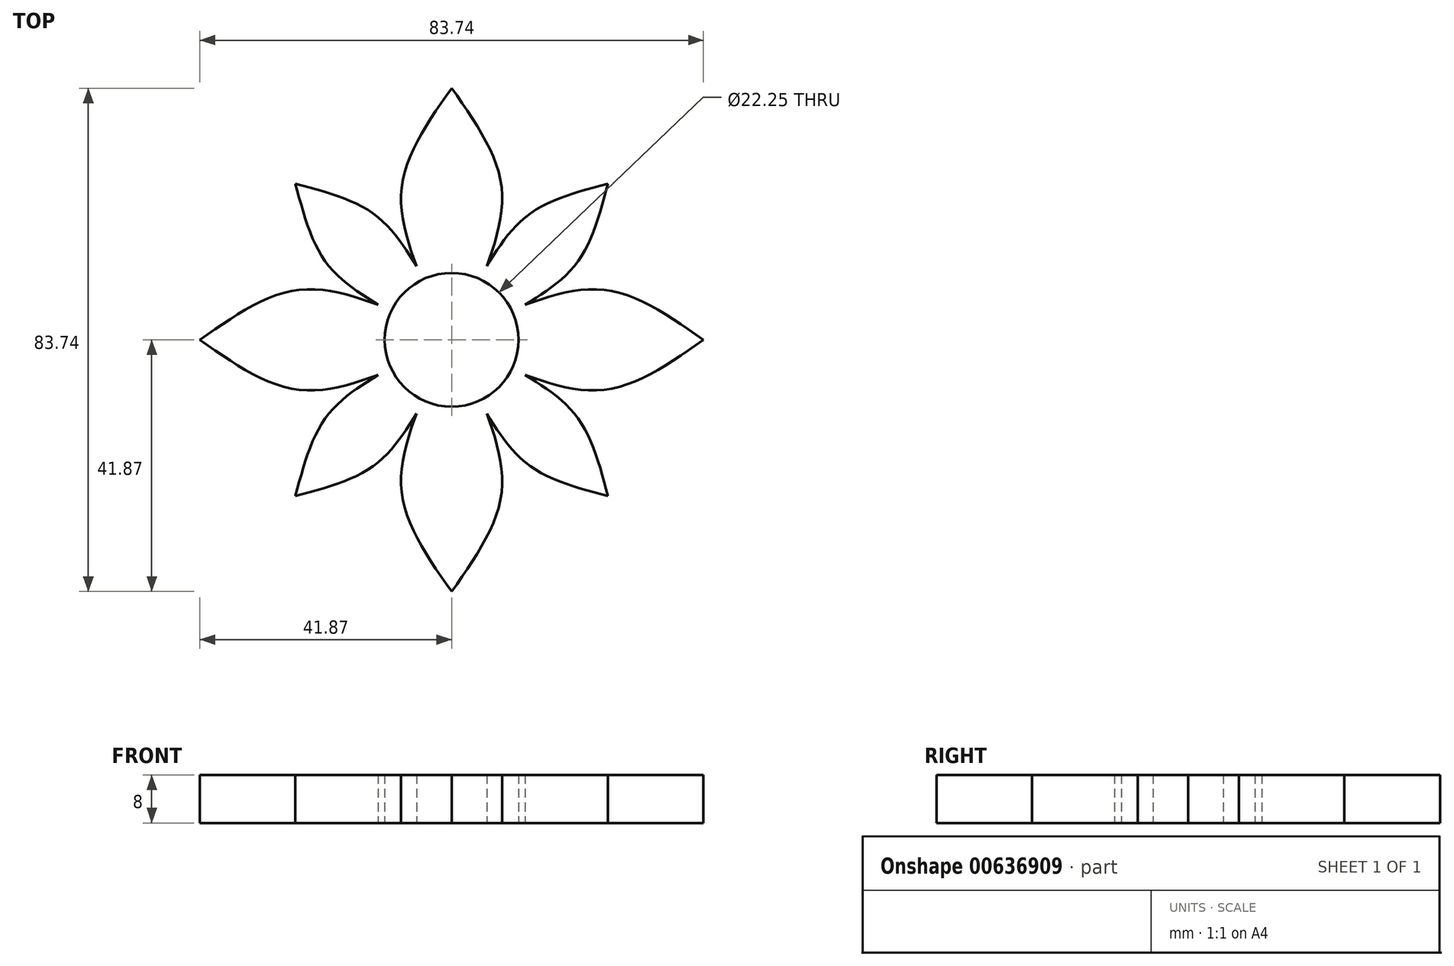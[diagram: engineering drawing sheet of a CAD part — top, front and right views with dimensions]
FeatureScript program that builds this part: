
annotation { "Feature Type Name" : "Feature", "Feature Type Description" : "" }
export const myFeature = defineFeature(function(context is Context, id is Id, definition is map)
    precondition{}
    {
        {
            var Q0;
            Q0=qCreatedBy(makeId("Top.planeOp"),FACE);
            var sketch = newSketch(context, id + "F0", { "sketchPlane" : qUnion([Q0])});
            skCircle(sketch, "E0", {"center": v(0, 0) * mm, "radius": 11.12 * mm});
            skCircle(sketch, "E1.cCircle", {"center": v(0, 26.05) * mm, "radius": 4.7 * mm, "construction": true});
            skLineSegment(sketch, "E1.0", {"start": v(5.41, 26.33) * mm, "end": v(2.95, 21.5) * mm});
            skLineSegment(sketch, "E1.1", {"start": v(2.95, 21.5) * mm, "end": v(-2.46, 21.22) * mm});
            skLineSegment(sketch, "E1.2", {"start": v(-2.46, 21.22) * mm, "end": v(-5.41, 25.77) * mm});
            skLineSegment(sketch, "E1.3", {"start": v(-5.41, 25.77) * mm, "end": v(-2.95, 30.6) * mm});
            skLineSegment(sketch, "E1.4", {"start": v(-2.95, 30.6) * mm, "end": v(2.46, 30.87) * mm});
            skLineSegment(sketch, "E1.5", {"start": v(2.46, 30.87) * mm, "end": v(5.41, 26.33) * mm});
            skPoint(sketch, "E1.0.midPoint", {"position": v(4.18, 23.91) * mm});
            skPoint(sketch, "E2.1.0", {"position": v(-23.91, 4.18) * mm});
            skCircle(sketch, "E2.1.1", {"center": v(-26.05, 0) * mm, "radius": 4.7 * mm, "construction": true});
            skLineSegment(sketch, "E2.1.2", {"start": v(-30.6, -2.95) * mm, "end": v(-30.87, 2.46) * mm});
            skLineSegment(sketch, "E2.1.3", {"start": v(-26.33, 5.41) * mm, "end": v(-21.5, 2.95) * mm});
            skLineSegment(sketch, "E2.1.4", {"start": v(-21.5, 2.95) * mm, "end": v(-21.22, -2.46) * mm});
            skLineSegment(sketch, "E2.1.5", {"start": v(-21.22, -2.46) * mm, "end": v(-25.77, -5.41) * mm});
            skLineSegment(sketch, "E2.1.6", {"start": v(-25.77, -5.41) * mm, "end": v(-30.6, -2.95) * mm});
            skLineSegment(sketch, "E2.1.7", {"start": v(-30.87, 2.46) * mm, "end": v(-26.33, 5.41) * mm});
            skPoint(sketch, "E2.2.0", {"position": v(-4.18, -23.91) * mm});
            skCircle(sketch, "E2.2.1", {"center": v(0, -26.05) * mm, "radius": 4.7 * mm, "construction": true});
            skLineSegment(sketch, "E2.2.2", {"start": v(2.95, -30.6) * mm, "end": v(-2.46, -30.87) * mm});
            skLineSegment(sketch, "E2.2.3", {"start": v(-5.41, -26.33) * mm, "end": v(-2.95, -21.5) * mm});
            skLineSegment(sketch, "E2.2.4", {"start": v(-2.95, -21.5) * mm, "end": v(2.46, -21.22) * mm});
            skLineSegment(sketch, "E2.2.5", {"start": v(2.46, -21.22) * mm, "end": v(5.41, -25.77) * mm});
            skLineSegment(sketch, "E2.2.6", {"start": v(5.41, -25.77) * mm, "end": v(2.95, -30.6) * mm});
            skLineSegment(sketch, "E2.2.7", {"start": v(-2.46, -30.87) * mm, "end": v(-5.41, -26.33) * mm});
            skPoint(sketch, "E2.3.0", {"position": v(23.91, -4.18) * mm});
            skCircle(sketch, "E2.3.1", {"center": v(26.05, 0) * mm, "radius": 4.7 * mm, "construction": true});
            skLineSegment(sketch, "E2.3.2", {"start": v(30.6, 2.95) * mm, "end": v(30.87, -2.46) * mm});
            skLineSegment(sketch, "E2.3.3", {"start": v(26.33, -5.41) * mm, "end": v(21.5, -2.95) * mm});
            skLineSegment(sketch, "E2.3.4", {"start": v(21.5, -2.95) * mm, "end": v(21.22, 2.46) * mm});
            skLineSegment(sketch, "E2.3.5", {"start": v(21.22, 2.46) * mm, "end": v(25.77, 5.41) * mm});
            skLineSegment(sketch, "E2.3.6", {"start": v(25.77, 5.41) * mm, "end": v(30.6, 2.95) * mm});
            skLineSegment(sketch, "E2.3.7", {"start": v(30.87, -2.46) * mm, "end": v(26.33, -5.41) * mm});
            skFitSpline(sketch, "E3", {"points": [v(-4.98, 9.95) * mm, v(-8.27, 25.7) * mm, v(0, 41.87) * mm], "startDerivative": vector(-12.29, 32.71) * mm, "endDerivative": vector(21.92, 31.12) * mm});
            skFitSpline(sketch, "E4.MirrorCS", {"points": [v(-4.98, 9.95) * mm, v(-8.27, 25.7) * mm, v(0, 41.87) * mm], "startDerivative": vector(-12.29, 32.71) * mm, "endDerivative": vector(21.92, 31.12) * mm});
            skFitSpline(sketch, "E5.MirrorCS", {"points": [v(-4.98, -9.95) * mm, v(-8.27, -25.7) * mm, v(0, -41.87) * mm], "startDerivative": vector(-12.29, -32.71) * mm, "endDerivative": vector(21.92, -31.12) * mm});
            skFitSpline(sketch, "E6.MirrorCS", {"points": [v(4.98, -9.95) * mm, v(8.27, -25.7) * mm, v(0, -41.87) * mm], "startDerivative": vector(12.29, -32.71) * mm, "endDerivative": vector(-21.92, -31.12) * mm});
            skFitSpline(sketch, "E7.MirrorCS", {"points": [v(4.98, -9.95) * mm, v(8.27, -25.7) * mm, v(0, -41.87) * mm], "startDerivative": vector(12.29, -32.71) * mm, "endDerivative": vector(-21.92, -31.12) * mm});
            skFitSpline(sketch, "E8.MirrorCS", {"points": [v(4.98, -9.95) * mm, v(8.27, -25.7) * mm, v(0, -41.87) * mm], "startDerivative": vector(12.29, -32.71) * mm, "endDerivative": vector(-21.92, -31.12) * mm});
            skFitSpline(sketch, "E9.MirrorCS", {"points": [v(-9.95, -4.98) * mm, v(-25.7, -8.27) * mm, v(-41.87, 0) * mm], "startDerivative": vector(-32.71, -12.29) * mm, "endDerivative": vector(-31.12, 21.92) * mm});
            skFitSpline(sketch, "E10.MirrorCS", {"points": [v(-9.95, 4.98) * mm, v(-25.7, 8.27) * mm, v(-41.87, 0) * mm], "startDerivative": vector(-32.71, 12.29) * mm, "endDerivative": vector(-31.12, -21.92) * mm});
            skFitSpline(sketch, "E11.MirrorCS", {"points": [v(9.95, 4.98) * mm, v(25.7, 8.27) * mm, v(41.87, 0) * mm], "startDerivative": vector(32.71, 12.29) * mm, "endDerivative": vector(31.12, -21.92) * mm});
            skFitSpline(sketch, "E12.MirrorCS", {"points": [v(9.95, -4.98) * mm, v(25.7, -8.27) * mm, v(41.87, 0) * mm], "startDerivative": vector(32.71, -12.29) * mm, "endDerivative": vector(31.12, 21.92) * mm});
            skFitSpline(sketch, "E13.MirrorCS", {"points": [v(4.98, 9.95) * mm, v(8.27, 25.7) * mm, v(0, 41.87) * mm], "startDerivative": vector(12.29, 32.71) * mm, "endDerivative": vector(-21.92, 31.12) * mm});
            skCircle(sketch, "E14", {"center": v(0, 0) * mm, "radius": 13.56 * mm});
            skPoint(sketch, "E15", {"position": v(12.24, 5.84) * mm});
            skPoint(sketch, "E16", {"position": v(5.84, 12.24) * mm});
            skPoint(sketch, "E17.1.internal.snap0", {"position": v(13, 13) * mm});
            skFitSpline(sketch, "E17", {"points": [v(5.84, 12.24) * mm, v(13, 20.97) * mm, v(25.99, 25.99) * mm], "startDerivative": vector(12.84, 20.52) * mm, "endDerivative": vector(27.2, 7.2) * mm});
            skFitSpline(sketch, "E18.MirrorCS", {"points": [v(12.24, 5.84) * mm, v(20.97, 13) * mm, v(25.99, 25.99) * mm], "startDerivative": vector(20.52, 12.84) * mm, "endDerivative": vector(7.2, 27.2) * mm});
            skFitSpline(sketch, "E19.MirrorCS", {"points": [v(-5.84, 12.24) * mm, v(-13, 20.97) * mm, v(-25.99, 25.99) * mm], "startDerivative": vector(-12.84, 20.52) * mm, "endDerivative": vector(-27.2, 7.2) * mm});
            skFitSpline(sketch, "E20.MirrorCS", {"points": [v(-12.24, 5.84) * mm, v(-20.97, 13) * mm, v(-25.99, 25.99) * mm], "startDerivative": vector(-20.52, 12.84) * mm, "endDerivative": vector(-7.2, 27.2) * mm});
            skFitSpline(sketch, "E21.MirrorCS", {"points": [v(-12.24, -5.84) * mm, v(-20.97, -13) * mm, v(-25.99, -25.99) * mm], "startDerivative": vector(-20.52, -12.84) * mm, "endDerivative": vector(-7.2, -27.2) * mm});
            skFitSpline(sketch, "E22.MirrorCS", {"points": [v(-5.84, -12.24) * mm, v(-13, -20.97) * mm, v(-25.99, -25.99) * mm], "startDerivative": vector(-12.84, -20.52) * mm, "endDerivative": vector(-27.2, -7.2) * mm});
            skFitSpline(sketch, "E23.MirrorCS", {"points": [v(5.84, -12.24) * mm, v(13, -20.97) * mm, v(25.99, -25.99) * mm], "startDerivative": vector(12.84, -20.52) * mm, "endDerivative": vector(27.2, -7.2) * mm});
            skFitSpline(sketch, "E24.MirrorCS", {"points": [v(12.24, -5.84) * mm, v(20.97, -13) * mm, v(25.99, -25.99) * mm], "startDerivative": vector(20.52, -12.84) * mm, "endDerivative": vector(7.2, -27.2) * mm});
            skSolve(sketch);
        }
        {
            var Q0;
            Q0=makeQuery(id+"F0.imprint","IMPRINT",FACE,{"disambiguationData":[TD([[makeQuery(id+"F0.imprint","IMPRINT",EDGE,{"derivedFrom":sQuery(id+"F0.wireOp",EDGE,"E2.1.2")}),-1.0]])]});
            var Q1;
            {var subQ5=sQuery(id+"F0.wireOp",EDGE,"E17");Q1=makeQuery(id+"F0.imprint","IMPRINT",FACE,{"disambiguationData":[TD([[makeQuery(id+"F0.imprint","IMPRINT",EDGE,{"derivedFrom":subQ5}),-1.0]])]});}
            var Q2;
            Q2=makeQuery(id+"F0.imprint","IMPRINT",FACE,{"disambiguationData":[TD([[makeQuery(id+"F0.imprint","IMPRINT",EDGE,{"derivedFrom":sQuery(id+"F0.wireOp",EDGE,"E2.2.2")}),-1.0]])]});
            var Q3;
            {var subQ0=sQuery(id+"F0.wireOp",EDGE,"E8.MirrorCS");var subQ1=sQuery(id+"F0.wireOp",EDGE,"E0");var subQ2=makeQuery(id+"F0.imprint","INTERSECT",VERTEX,{"derivedFrom":[subQ1,subQ0]});Q3=makeQuery(id+"F0.imprint","IMPRINT",FACE,{"disambiguationData":[TD([[makeQuery(id+"F0.imprint","IMPRINT",EDGE,{"disambiguationData":[TD([[subQ2,-1.0]])],"derivedFrom":subQ1}),-1.0]])]});}
            var Q4;
            {var subQ5=sQuery(id+"F0.wireOp",EDGE,"E23.MirrorCS");Q4=makeQuery(id+"F0.imprint","IMPRINT",FACE,{"disambiguationData":[TD([[makeQuery(id+"F0.imprint","IMPRINT",EDGE,{"derivedFrom":subQ5}),1.0]])]});}
            var Q5;
            Q5=makeQuery(id+"F0.imprint","IMPRINT",FACE,{"disambiguationData":[TD([[makeQuery(id+"F0.imprint","IMPRINT",EDGE,{"derivedFrom":sQuery(id+"F0.wireOp",EDGE,"E2.2.2")}),1.0]])]});
            var Q6;
            Q6=makeQuery(id+"F0.imprint","IMPRINT",FACE,{"disambiguationData":[TD([[makeQuery(id+"F0.imprint","IMPRINT",EDGE,{"derivedFrom":sQuery(id+"F0.wireOp",EDGE,"E1.0")}),1.0]])]});
            var Q7;
            Q7=makeQuery(id+"F0.imprint","IMPRINT",FACE,{"disambiguationData":[TD([[makeQuery(id+"F0.imprint","IMPRINT",EDGE,{"derivedFrom":sQuery(id+"F0.wireOp",EDGE,"E2.3.2")}),-1.0]])]});
            var Q8;
            {var subQ0=sQuery(id+"F0.wireOp",EDGE,"E11.MirrorCS");var subQ1=sQuery(id+"F0.wireOp",EDGE,"E0");var subQ2=makeQuery(id+"F0.imprint","INTERSECT",VERTEX,{"derivedFrom":[subQ1,subQ0]});Q8=makeQuery(id+"F0.imprint","IMPRINT",FACE,{"disambiguationData":[TD([[makeQuery(id+"F0.imprint","IMPRINT",EDGE,{"disambiguationData":[TD([[subQ2,1.0]])],"derivedFrom":subQ1}),-1.0]])]});}
            var Q9;
            {var subQ0=sQuery(id+"F0.wireOp",EDGE,"E5.MirrorCS");var subQ1=sQuery(id+"F0.wireOp",EDGE,"E0");var subQ2=makeQuery(id+"F0.imprint","INTERSECT",VERTEX,{"derivedFrom":[subQ1,subQ0]});Q9=makeQuery(id+"F0.imprint","IMPRINT",FACE,{"disambiguationData":[TD([[makeQuery(id+"F0.imprint","IMPRINT",EDGE,{"disambiguationData":[TD([[subQ2,-1.0]])],"derivedFrom":subQ1}),-1.0]])]});}
            var Q10;
            {var subQ0=sQuery(id+"F0.wireOp",EDGE,"E0");var subQ4=makeQuery(id+"F0.imprint","INTERSECT",VERTEX,{"derivedFrom":[subQ0,sQuery(id+"F0.wireOp",EDGE,"E13.MirrorCS")]});Q10=makeQuery(id+"F0.imprint","IMPRINT",FACE,{"disambiguationData":[TD([[makeQuery(id+"F0.imprint","IMPRINT",EDGE,{"disambiguationData":[TD([[subQ4,1.0]])],"derivedFrom":subQ0}),1.0]])]});}
            var Q11;
            {var subQ0=sQuery(id+"F0.wireOp",EDGE,"E5.MirrorCS");var subQ1=sQuery(id+"F0.wireOp",EDGE,"E0");var subQ2=makeQuery(id+"F0.imprint","INTERSECT",VERTEX,{"derivedFrom":[subQ1,subQ0]});Q11=makeQuery(id+"F0.imprint","IMPRINT",FACE,{"disambiguationData":[TD([[makeQuery(id+"F0.imprint","IMPRINT",EDGE,{"disambiguationData":[TD([[subQ2,1.0]])],"derivedFrom":subQ1}),-1.0]])]});}
            var Q12;
            {var subQ5=sQuery(id+"F0.wireOp",EDGE,"E22.MirrorCS");Q12=makeQuery(id+"F0.imprint","IMPRINT",FACE,{"disambiguationData":[TD([[makeQuery(id+"F0.imprint","IMPRINT",EDGE,{"derivedFrom":subQ5}),-1.0]])]});}
            var Q13;
            {var subQ5=sQuery(id+"F0.wireOp",EDGE,"E19.MirrorCS");Q13=makeQuery(id+"F0.imprint","IMPRINT",FACE,{"disambiguationData":[TD([[makeQuery(id+"F0.imprint","IMPRINT",EDGE,{"derivedFrom":subQ5}),1.0]])]});}
            var Q14;
            Q14=makeQuery(id+"F0.imprint","IMPRINT",FACE,{"disambiguationData":[TD([[makeQuery(id+"F0.imprint","IMPRINT",EDGE,{"derivedFrom":sQuery(id+"F0.wireOp",EDGE,"E2.1.2")}),1.0]])]});
            var Q15;
            Q15=makeQuery(id+"F0.imprint","IMPRINT",FACE,{"disambiguationData":[TD([[makeQuery(id+"F0.imprint","IMPRINT",EDGE,{"derivedFrom":sQuery(id+"F0.wireOp",EDGE,"E1.0")}),-1.0]])]});
            var Q16;
            {var subQ0=sQuery(id+"F0.wireOp",EDGE,"E4.MirrorCS");var subQ1=sQuery(id+"F0.wireOp",EDGE,"E0");var subQ2=makeQuery(id+"F0.imprint","INTERSECT",VERTEX,{"derivedFrom":[subQ1,subQ0]});Q16=makeQuery(id+"F0.imprint","IMPRINT",FACE,{"disambiguationData":[TD([[makeQuery(id+"F0.imprint","IMPRINT",EDGE,{"disambiguationData":[TD([[subQ2,-1.0]])],"derivedFrom":subQ1}),-1.0]])]});}
            var Q17;
            {var subQ0=sQuery(id+"F0.wireOp",EDGE,"E13.MirrorCS");var subQ1=sQuery(id+"F0.wireOp",EDGE,"E0");var subQ2=makeQuery(id+"F0.imprint","INTERSECT",VERTEX,{"derivedFrom":[subQ1,subQ0]});Q17=makeQuery(id+"F0.imprint","IMPRINT",FACE,{"disambiguationData":[TD([[makeQuery(id+"F0.imprint","IMPRINT",EDGE,{"disambiguationData":[TD([[subQ2,1.0]])],"derivedFrom":subQ1}),-1.0]])]});}
            var Q18;
            Q18=makeQuery(id+"F0.imprint","IMPRINT",FACE,{"disambiguationData":[TD([[makeQuery(id+"F0.imprint","IMPRINT",EDGE,{"derivedFrom":sQuery(id+"F0.wireOp",EDGE,"E2.3.2")}),1.0]])]});
            var Q19;
            {var subQ0=sQuery(id+"F0.wireOp",EDGE,"E4.MirrorCS");var subQ1=sQuery(id+"F0.wireOp",EDGE,"E0");var subQ2=makeQuery(id+"F0.imprint","INTERSECT",VERTEX,{"derivedFrom":[subQ1,subQ0]});Q19=makeQuery(id+"F0.imprint","IMPRINT",FACE,{"disambiguationData":[TD([[makeQuery(id+"F0.imprint","IMPRINT",EDGE,{"disambiguationData":[TD([[subQ2,1.0]])],"derivedFrom":subQ1}),-1.0]])]});}
            var Q20;
            {var subQ2=sQuery(id+"F0.wireOp",EDGE,"E10.MirrorCS");var subQ4=sQuery(id+"F0.wireOp",EDGE,"E0");var subQ5=makeQuery(id+"F0.imprint","INTERSECT",VERTEX,{"derivedFrom":[subQ4,subQ2]});Q20=makeQuery(id+"F0.imprint","IMPRINT",FACE,{"disambiguationData":[TD([[makeQuery(id+"F0.imprint","IMPRINT",EDGE,{"disambiguationData":[TD([[subQ5,-1.0]])],"derivedFrom":subQ4}),-1.0]])]});}
            var Q21;
            {var subQ0=sQuery(id+"F0.wireOp",EDGE,"E20.MirrorCS");var subQ1=sQuery(id+"F0.wireOp",EDGE,"E10.MirrorCS");var subQ2=makeQuery(id+"F0.imprint","INTERSECT",VERTEX,{"derivedFrom":[subQ1,subQ0]});Q21=makeQuery(id+"F0.imprint","IMPRINT",FACE,{"disambiguationData":[TD([[makeQuery(id+"F0.imprint","IMPRINT",EDGE,{"disambiguationData":[TD([[subQ2,1.0]])],"derivedFrom":subQ1}),1.0]])]});}
            var Q22;
            {var subQ0=sQuery(id+"F0.wireOp",EDGE,"E21.MirrorCS");var subQ1=sQuery(id+"F0.wireOp",EDGE,"E9.MirrorCS");var subQ2=makeQuery(id+"F0.imprint","INTERSECT",VERTEX,{"derivedFrom":[subQ1,subQ0]});Q22=makeQuery(id+"F0.imprint","IMPRINT",FACE,{"disambiguationData":[TD([[makeQuery(id+"F0.imprint","IMPRINT",EDGE,{"disambiguationData":[TD([[subQ2,1.0]])],"derivedFrom":subQ1}),-1.0]])]});}
            var Q23;
            {var subQ0=sQuery(id+"F0.wireOp",EDGE,"E24.MirrorCS");var subQ1=sQuery(id+"F0.wireOp",EDGE,"E12.MirrorCS");var subQ2=makeQuery(id+"F0.imprint","INTERSECT",VERTEX,{"derivedFrom":[subQ1,subQ0]});Q23=makeQuery(id+"F0.imprint","IMPRINT",FACE,{"disambiguationData":[TD([[makeQuery(id+"F0.imprint","IMPRINT",EDGE,{"disambiguationData":[TD([[subQ2,1.0]])],"derivedFrom":subQ1}),1.0]])]});}
            var Q24;
            {var subQ0=sQuery(id+"F0.wireOp",EDGE,"E18.MirrorCS");var subQ1=sQuery(id+"F0.wireOp",EDGE,"E11.MirrorCS");var subQ2=makeQuery(id+"F0.imprint","INTERSECT",VERTEX,{"derivedFrom":[subQ1,subQ0]});Q24=makeQuery(id+"F0.imprint","IMPRINT",FACE,{"disambiguationData":[TD([[makeQuery(id+"F0.imprint","IMPRINT",EDGE,{"disambiguationData":[TD([[subQ2,1.0]])],"derivedFrom":subQ1}),-1.0]])]});}
            extrude(context, id + "F1", {"entities" : qUnion([Q0, Q1, Q2, Q3, Q4, Q5, Q6, Q7, Q8, Q9, Q10, Q11, Q12, Q13, Q14, Q15, Q16, Q17, Q18, Q19, Q20, Q21, Q22, Q23, Q24]), "depth" : 8 * mm, "offsetDistance" : 25 * mm});
        }
        {
            var Q0;
            Q0=qCreatedBy(makeId("Top.planeOp"),FACE);
            var sketch = newSketch(context, id + "F2", { "sketchPlane" : qUnion([Q0])});
            skCircle(sketch, "E25", {"center": v(0, 0) * mm, "radius": 11.12 * mm});
            skPoint(sketch, "E26", {"position": v(25.46, 0) * mm});
            skCircle(sketch, "E27.cCircle", {"center": v(25.46, 0) * mm, "radius": 4.1 * mm, "construction": true});
            skLineSegment(sketch, "E27.0", {"start": v(29.7, -2.1) * mm, "end": v(25.77, -4.73) * mm});
            skLineSegment(sketch, "E27.1", {"start": v(25.77, -4.73) * mm, "end": v(21.52, -2.63) * mm});
            skLineSegment(sketch, "E27.2", {"start": v(21.52, -2.63) * mm, "end": v(21.22, 2.1) * mm});
            skLineSegment(sketch, "E27.3", {"start": v(21.22, 2.1) * mm, "end": v(25.16, 4.73) * mm});
            skLineSegment(sketch, "E27.4", {"start": v(25.16, 4.73) * mm, "end": v(29.4, 2.63) * mm});
            skLineSegment(sketch, "E27.5", {"start": v(29.4, 2.63) * mm, "end": v(29.7, -2.1) * mm});
            skPoint(sketch, "E27.0.midPoint", {"position": v(27.74, -3.41) * mm});
            skPoint(sketch, "E28.1.0", {"position": v(3.41, 27.74) * mm});
            skPoint(sketch, "E28.1.1", {"position": v(0, 25.46) * mm});
            skCircle(sketch, "E28.1.2", {"center": v(0, 25.46) * mm, "radius": 4.1 * mm, "construction": true});
            skLineSegment(sketch, "E28.1.3", {"start": v(2.63, 21.52) * mm, "end": v(-2.1, 21.22) * mm});
            skLineSegment(sketch, "E28.1.4", {"start": v(-2.63, 29.4) * mm, "end": v(2.1, 29.7) * mm});
            skLineSegment(sketch, "E28.1.5", {"start": v(4.73, 25.77) * mm, "end": v(2.63, 21.52) * mm});
            skLineSegment(sketch, "E28.1.6", {"start": v(2.1, 29.7) * mm, "end": v(4.73, 25.77) * mm});
            skLineSegment(sketch, "E28.1.7", {"start": v(-2.1, 21.22) * mm, "end": v(-4.73, 25.16) * mm});
            skLineSegment(sketch, "E28.1.8", {"start": v(-4.73, 25.16) * mm, "end": v(-2.63, 29.4) * mm});
            skPoint(sketch, "E28.2.0", {"position": v(-27.74, 3.41) * mm});
            skPoint(sketch, "E28.2.1", {"position": v(-25.46, 0) * mm});
            skCircle(sketch, "E28.2.2", {"center": v(-25.46, 0) * mm, "radius": 4.1 * mm, "construction": true});
            skLineSegment(sketch, "E28.2.3", {"start": v(-21.52, 2.63) * mm, "end": v(-21.22, -2.1) * mm});
            skLineSegment(sketch, "E28.2.4", {"start": v(-29.4, -2.63) * mm, "end": v(-29.7, 2.1) * mm});
            skLineSegment(sketch, "E28.2.5", {"start": v(-25.77, 4.73) * mm, "end": v(-21.52, 2.63) * mm});
            skLineSegment(sketch, "E28.2.6", {"start": v(-29.7, 2.1) * mm, "end": v(-25.77, 4.73) * mm});
            skLineSegment(sketch, "E28.2.7", {"start": v(-21.22, -2.1) * mm, "end": v(-25.16, -4.73) * mm});
            skLineSegment(sketch, "E28.2.8", {"start": v(-25.16, -4.73) * mm, "end": v(-29.4, -2.63) * mm});
            skPoint(sketch, "E28.3.0", {"position": v(-3.41, -27.74) * mm});
            skPoint(sketch, "E28.3.1", {"position": v(0, -25.46) * mm});
            skCircle(sketch, "E28.3.2", {"center": v(0, -25.46) * mm, "radius": 4.1 * mm, "construction": true});
            skLineSegment(sketch, "E28.3.3", {"start": v(-2.63, -21.52) * mm, "end": v(2.1, -21.22) * mm});
            skLineSegment(sketch, "E28.3.4", {"start": v(2.63, -29.4) * mm, "end": v(-2.1, -29.7) * mm});
            skLineSegment(sketch, "E28.3.5", {"start": v(-4.73, -25.77) * mm, "end": v(-2.63, -21.52) * mm});
            skLineSegment(sketch, "E28.3.6", {"start": v(-2.1, -29.7) * mm, "end": v(-4.73, -25.77) * mm});
            skLineSegment(sketch, "E28.3.7", {"start": v(2.1, -21.22) * mm, "end": v(4.73, -25.16) * mm});
            skLineSegment(sketch, "E28.3.8", {"start": v(4.73, -25.16) * mm, "end": v(2.63, -29.4) * mm});
            skSolve(sketch);
        }
        {
            var Q0;
            Q0=sQuery(id+"F2.wireOp",VERTEX,"E25.center");
            var Q1;
            Q1=makeQuery(id+"F1.opExtrude","SWEPT_BODY",BODY,{"disambiguationData":[OSD([sQuery(id+"F0.wireOp",EDGE,"E4.MirrorCS"),sQuery(id+"F0.wireOp",EDGE,"E5.MirrorCS"),sQuery(id+"F0.wireOp",EDGE,"E8.MirrorCS"),sQuery(id+"F0.wireOp",EDGE,"E9.MirrorCS"),sQuery(id+"F0.wireOp",EDGE,"E10.MirrorCS"),sQuery(id+"F0.wireOp",EDGE,"E11.MirrorCS"),sQuery(id+"F0.wireOp",EDGE,"E12.MirrorCS"),sQuery(id+"F0.wireOp",EDGE,"E13.MirrorCS"),sQuery(id+"F0.wireOp",EDGE,"E17"),sQuery(id+"F0.wireOp",EDGE,"E18.MirrorCS"),sQuery(id+"F0.wireOp",EDGE,"E19.MirrorCS"),sQuery(id+"F0.wireOp",EDGE,"E20.MirrorCS"),sQuery(id+"F0.wireOp",EDGE,"E21.MirrorCS"),sQuery(id+"F0.wireOp",EDGE,"E22.MirrorCS"),sQuery(id+"F0.wireOp",EDGE,"E23.MirrorCS"),sQuery(id+"F0.wireOp",EDGE,"E24.MirrorCS")])]});
            hole(context, id + "F3", {"style" : HoleStyle.SIMPLE, "endStyle" : HoleEndStyle.THROUGH, "oppositeDirection" : true, "holeDiameter" : 22.25 * mm, "majorDiameter" : 5 * mm, "isTappedThrough" : true, "tappedDepth" : 12 * mm, "tapClearance" : 3, "locations" : qUnion([Q0]), "scope" : qUnion([Q1])});
        }
    });
